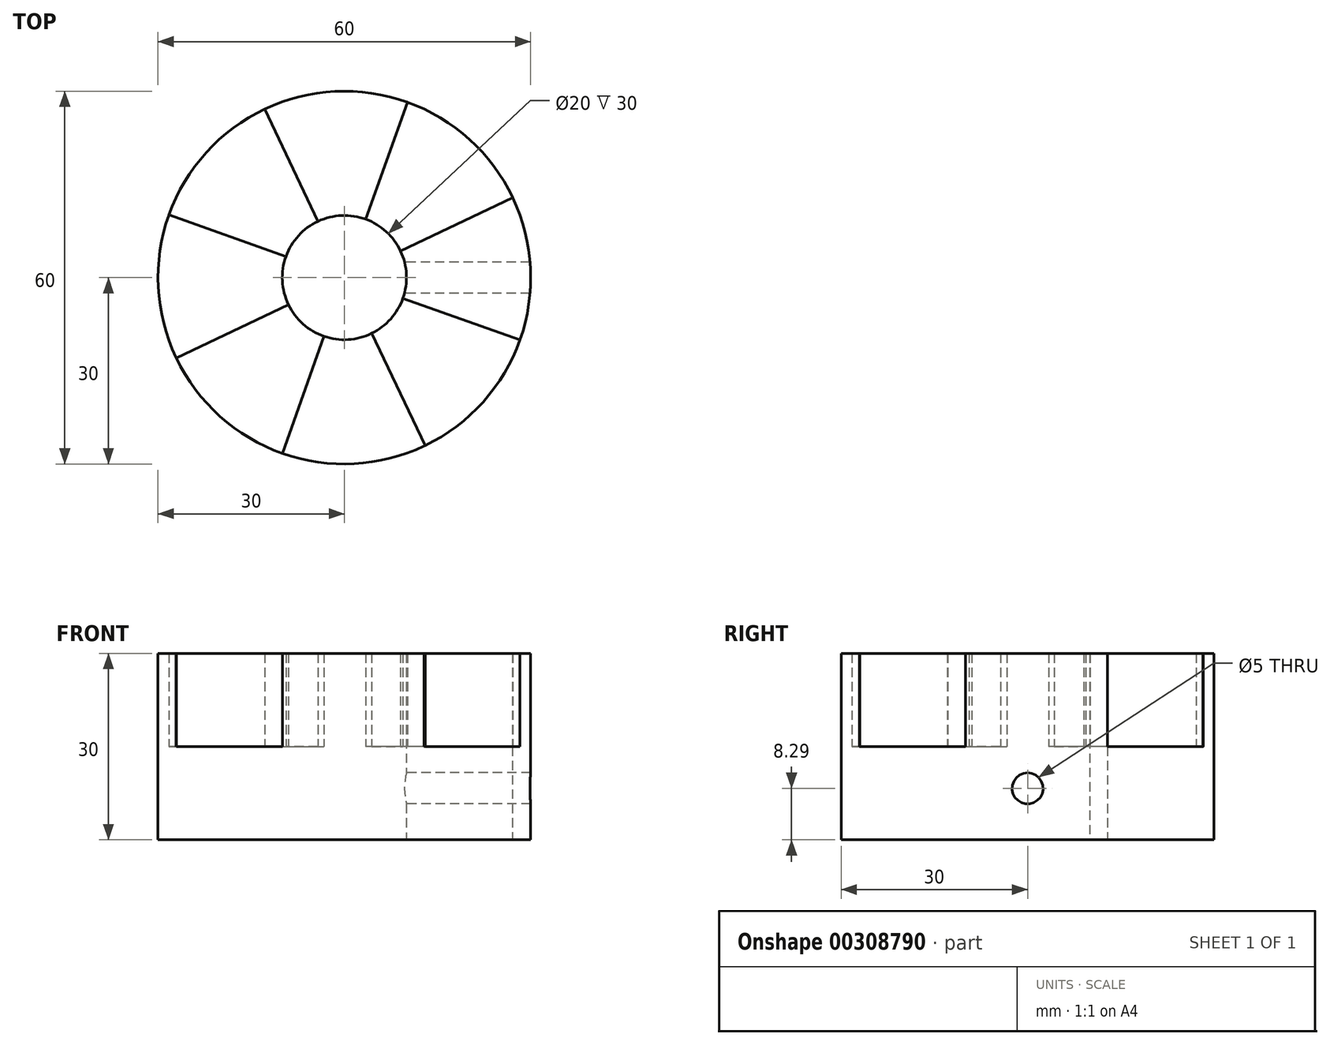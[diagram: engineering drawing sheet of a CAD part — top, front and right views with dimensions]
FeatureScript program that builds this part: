
annotation { "Feature Type Name" : "Feature", "Feature Type Description" : "" }
export const myFeature = defineFeature(function(context is Context, id is Id, definition is map)
    precondition{}
    {
        {
            var Q0;
            Q0=qCreatedBy(makeId("Top.planeOp"),FACE);
            var sketch = newSketch(context, id + "F0", { "sketchPlane" : qUnion([Q0])});
            skCircle(sketch, "E0", {"center": v(0, 0) * mm, "radius": 10 * mm});
            skCircle(sketch, "E1", {"center": v(0, 0) * mm, "radius": 30 * mm});
            skLineSegment(sketch, "E2.0", {"start": v(27.1, 12.85) * mm, "end": v(27.06, 12.85) * mm});
            skLineSegment(sketch, "E3.0", {"start": v(28.27, -10.05) * mm, "end": v(28.23, -10.05) * mm});
            skLineSegment(sketch, "E4.1.0", {"start": v(10.08, 28.26) * mm, "end": v(10.05, 28.23) * mm});
            skLineSegment(sketch, "E4.1.1", {"start": v(27.1, 12.88) * mm, "end": v(27.06, 12.85) * mm});
            skLineSegment(sketch, "E4.2.1", {"start": v(10.05, 28.27) * mm, "end": v(10.05, 28.23) * mm});
            skLineSegment(sketch, "E4.3.0", {"start": v(-28.26, 10.08) * mm, "end": v(-28.23, 10.05) * mm});
            skLineSegment(sketch, "E4.4.0", {"start": v(-27.1, -12.85) * mm, "end": v(-27.06, -12.85) * mm});
            skLineSegment(sketch, "E4.4.1", {"start": v(-28.27, 10.05) * mm, "end": v(-28.23, 10.05) * mm});
            skLineSegment(sketch, "E4.5.0", {"start": v(-10.08, -28.26) * mm, "end": v(-10.05, -28.23) * mm});
            skLineSegment(sketch, "E4.5.1", {"start": v(-27.1, -12.88) * mm, "end": v(-27.06, -12.85) * mm});
            skLineSegment(sketch, "E4.6.0", {"start": v(12.85, -27.1) * mm, "end": v(12.85, -27.06) * mm});
            skLineSegment(sketch, "E4.6.1", {"start": v(-10.05, -28.27) * mm, "end": v(-10.05, -28.23) * mm});
            skLineSegment(sketch, "E4.7.0", {"start": v(28.26, -10.08) * mm, "end": v(28.23, -10.05) * mm});
            skLineSegment(sketch, "E4.7.1", {"start": v(12.88, -27.1) * mm, "end": v(12.85, -27.06) * mm});
            skLineSegment(sketch, "E5", {"start": v(9.03, 4.3) * mm, "end": v(27.1, 12.87) * mm});
            skLineSegment(sketch, "E6", {"start": v(9.43, -3.34) * mm, "end": v(28.28, -10.01) * mm});
            skPoint(sketch, "E7.orphan", {"position": v(18.55, 36.7) * mm});
            skPoint(sketch, "E8.orphan", {"position": v(12.9, 1.68) * mm});
            skPoint(sketch, "E9.orphan", {"position": v(-7.07, -7.07) * mm});
            skPoint(sketch, "E10.orphan", {"position": v(-7.94, -10.31) * mm});
            skPoint(sketch, "E11.orphan", {"position": v(40.73, -10.05) * mm});
            skPoint(sketch, "E12.orphan", {"position": v(36.7, -18.55) * mm});
            skPoint(sketch, "E13.orphan", {"position": v(35.9, 21.7) * mm});
            skPoint(sketch, "E14.orphan", {"position": v(39.07, 12.83) * mm});
            skPoint(sketch, "E15.orphan", {"position": v(40.75, 0) * mm});
            skPoint(sketch, "E16.orphan", {"position": v(10.05, 40.73) * mm});
            skPoint(sketch, "E17.orphan", {"position": v(-12.83, 39.07) * mm});
            skPoint(sketch, "E18.orphan", {"position": v(-21.7, 35.9) * mm});
            skPoint(sketch, "E19.orphan", {"position": v(-36.7, 18.55) * mm});
            skPoint(sketch, "E20.orphan", {"position": v(-40.73, 10.05) * mm});
            skPoint(sketch, "E21.orphan", {"position": v(-39.07, -12.83) * mm});
            skPoint(sketch, "E22.orphan", {"position": v(-35.9, -21.7) * mm});
            skPoint(sketch, "E23.orphan", {"position": v(12.83, -39.07) * mm});
            skPoint(sketch, "E24.orphan", {"position": v(21.7, -35.9) * mm});
            skPoint(sketch, "E25.orphan", {"position": v(-18.55, -36.7) * mm});
            skPoint(sketch, "E26.orphan", {"position": v(-10.05, -40.73) * mm});
            skLineSegment(sketch, "E27.1.0", {"start": v(-4.25, 9.05) * mm, "end": v(-12.83, 27.12) * mm});
            skLineSegment(sketch, "E27.1.1", {"start": v(3.46, 9.38) * mm, "end": v(10.14, 28.23) * mm});
            skLineSegment(sketch, "E27.2.0", {"start": v(-9, -4.37) * mm, "end": v(-27.06, -12.95) * mm});
            skLineSegment(sketch, "E27.2.1", {"start": v(-9.4, 3.4) * mm, "end": v(-28.26, 10.08) * mm});
            skLineSegment(sketch, "E27.3.0", {"start": v(4.42, -8.97) * mm, "end": v(13, -27.04) * mm});
            skLineSegment(sketch, "E27.3.1", {"start": v(-3.28, -9.45) * mm, "end": v(-9.95, -28.3) * mm});
            skPoint(sketch, "E27.center", {"position": v(0.1, 0) * mm});
            skPoint(sketch, "E28.orphan", {"position": v(-4.19, 8.93) * mm});
            skPoint(sketch, "E29.orphan", {"position": v(3.44, 9.32) * mm});
            skPoint(sketch, "E30.orphan", {"position": v(-9.22, 3.34) * mm});
            skPoint(sketch, "E31.orphan", {"position": v(-8.82, -4.3) * mm});
            skPoint(sketch, "E32.orphan", {"position": v(-3.23, -9.32) * mm});
            skPoint(sketch, "E33.orphan", {"position": v(4.4, -8.93) * mm});
            skPoint(sketch, "E34.orphan", {"position": v(-28.07, 10.01) * mm});
            skPoint(sketch, "E35.orphan", {"position": v(-12.77, 27) * mm});
            skPoint(sketch, "E36.orphan", {"position": v(10.12, 28.18) * mm});
            skPoint(sketch, "E37.orphan", {"position": v(-9.9, -28.17) * mm});
            skPoint(sketch, "E38.orphan", {"position": v(-26.89, -12.87) * mm});
            skPoint(sketch, "E39.orphan", {"position": v(12.98, -27) * mm});
            skPoint(sketch, "E40.orphan", {"position": v(28.28, -10.01) * mm});
            skSolve(sketch);
        }
        {
            var Q0;
            Q0 = qSketchRegion(id + "F0", true);
            extrude(context, id + "F1", {"entities" : qUnion([Q0]), "depth" : 15 * mm});
        }
        {
            var Q0;
            Q0=qCreatedBy(makeId("Right.planeOp"),FACE);
            var sketch = newSketch(context, id + "F2", { "sketchPlane" : qUnion([Q0])});
            skCircle(sketch, "E41", {"center": v(0, 8.29) * mm, "radius": 2.5 * mm});
            skSolve(sketch);
        }
        {
            var Q0;
            {var subQ0=sQuery(id+"F0.wireOp",EDGE,"E4.1.0");Q0=makeQuery(id+"F0.imprint","IMPRINT",FACE,{"disambiguationData":[TD([[makeQuery(id+"F0.imprint","IMPRINT",EDGE,{"derivedFrom":subQ0}),1.0]])]});}
            var Q1;
            {var subQ0=sQuery(id+"F0.wireOp",EDGE,"E4.6.0");Q1=makeQuery(id+"F0.imprint","IMPRINT",FACE,{"disambiguationData":[TD([[makeQuery(id+"F0.imprint","IMPRINT",EDGE,{"derivedFrom":subQ0}),1.0]])]});}
            var Q2;
            {var subQ5=sQuery(id+"F0.wireOp",EDGE,"E4.3.0");Q2=makeQuery(id+"F0.imprint","IMPRINT",FACE,{"disambiguationData":[TD([[makeQuery(id+"F0.imprint","IMPRINT",EDGE,{"derivedFrom":subQ5}),1.0]])]});}
            var Q3;
            {var subQ6=sQuery(id+"F0.wireOp",EDGE,"E6");Q3=makeQuery(id+"F0.imprint","IMPRINT",FACE,{"disambiguationData":[TD([[makeQuery(id+"F0.imprint","IMPRINT",EDGE,{"derivedFrom":subQ6}),1.0]])]});}
            extrude(context, id + "F3", {"entities" : qUnion([Q0, Q1, Q2, Q3]), "operationType" : NewBodyOperationType.ADD, "depth" : 30 * mm});
        }
        {
            var Q0;
            Q0 = qSketchRegion(id + "F2", true);
            extrude(context, id + "F4", {"entities" : qUnion([Q0]), "operationType" : NewBodyOperationType.REMOVE, "depth" : 34 * mm});
        }
    });
